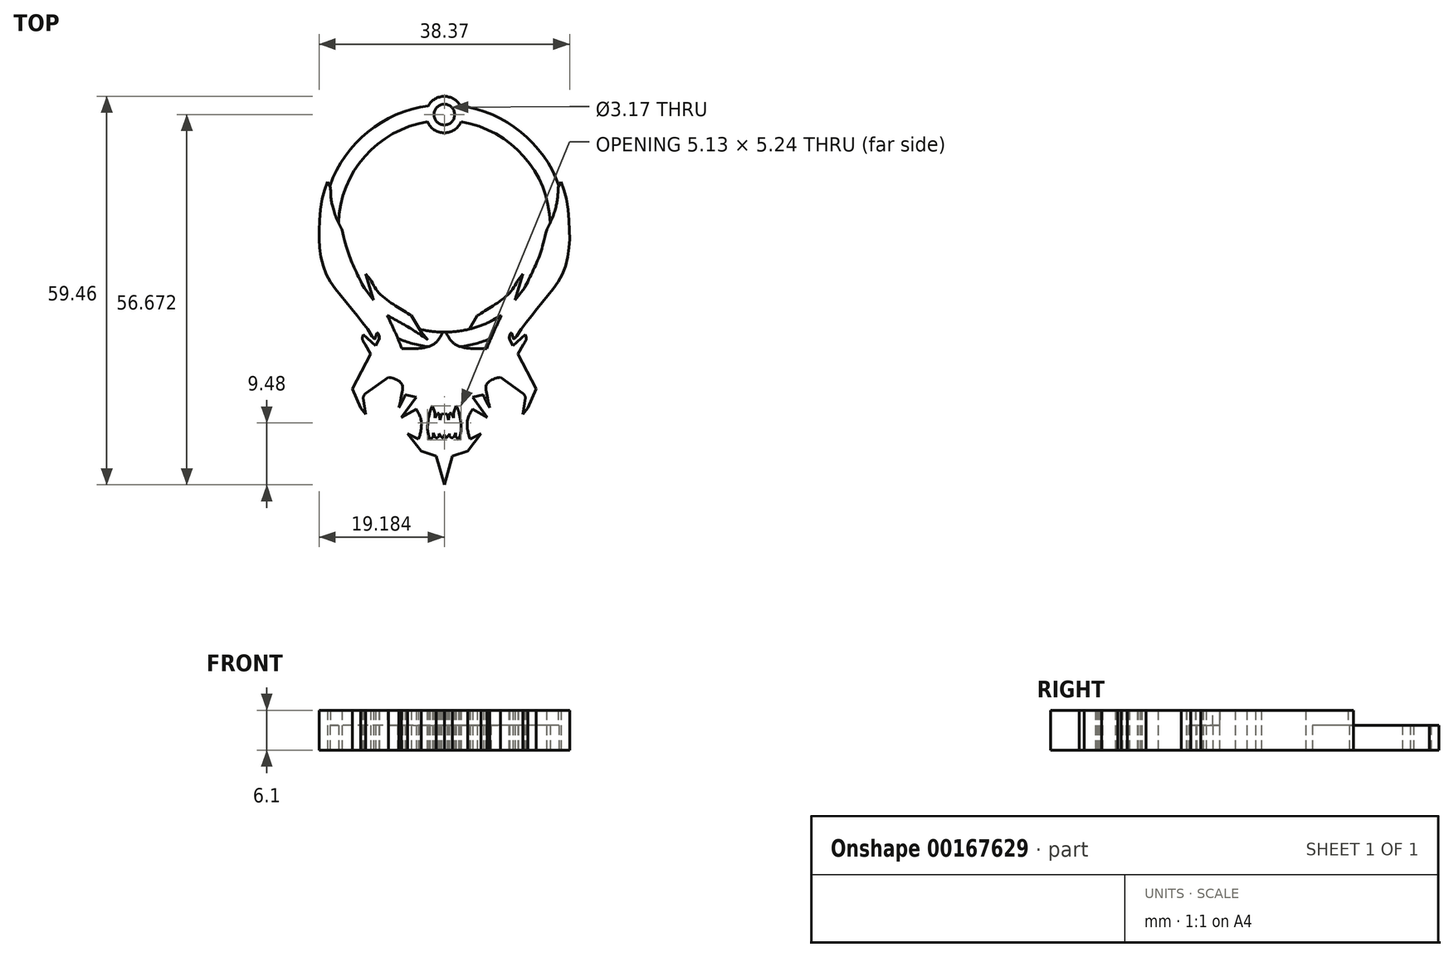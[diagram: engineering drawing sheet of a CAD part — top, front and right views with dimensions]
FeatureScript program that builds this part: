
annotation { "Feature Type Name" : "Feature", "Feature Type Description" : "" }
export const myFeature = defineFeature(function(context is Context, id is Id, definition is map)
    precondition{}
    {
        {
            var Q0;
            Q0=qCreatedBy(makeId("Top.planeOp"),FACE);
            var sketch = newSketch(context, id + "F0", { "sketchPlane" : qUnion([Q0])});
            skLineSegment(sketch, "E0", {"start": v(-0.9, 16.54) * mm, "end": v(-0.9, -34.26) * mm});
            skLineSegment(sketch, "E1", {"start": v(-18.76, 15.36) * mm, "end": v(-18.33, 14.53) * mm});
            skLineSegment(sketch, "E2", {"start": v(-12.92, 1.26) * mm, "end": v(-12.21, 0.39) * mm});
            skLineSegment(sketch, "E3", {"start": v(-5.97, -5.12) * mm, "end": v(-4.46, -7.6) * mm});
            skLineSegment(sketch, "E4", {"start": v(-4.46, -7.6) * mm, "end": v(-3.4, -8.82) * mm});
            skLineSegment(sketch, "E5", {"start": v(-13.17, -0.94) * mm, "end": v(-11.72, -2.75) * mm});
            skLineSegment(sketch, "E6", {"start": v(-11.72, -2.75) * mm, "end": v(-12.92, 1.26) * mm});
            skLineSegment(sketch, "E7", {"start": v(-11.4, -9.73) * mm, "end": v(-13.3, -8.03) * mm});
            skLineSegment(sketch, "E8", {"start": v(-11.4, -9.73) * mm, "end": v(-10.9, -8.8) * mm});
            skLineSegment(sketch, "E9", {"start": v(-12.99, -9.53) * mm, "end": v(-12.17, -10.97) * mm});
            skLineSegment(sketch, "E10", {"start": v(-12.17, -10.97) * mm, "end": v(-15, -16.37) * mm});
            skLineSegment(sketch, "E11", {"start": v(-15, -16.37) * mm, "end": v(-13.72, -19.25) * mm});
            skLineSegment(sketch, "E12", {"start": v(-13.72, -19.25) * mm, "end": v(-12.93, -20.2) * mm});
            skLineSegment(sketch, "E13", {"start": v(-12.93, -20.2) * mm, "end": v(-13.32, -17.75) * mm});
            skLineSegment(sketch, "E14", {"start": v(-7.49, -20.73) * mm, "end": v(-5.22, -19.47) * mm});
            skLineSegment(sketch, "E15", {"start": v(-6.52, -23.2) * mm, "end": v(-4.85, -24.02) * mm});
            skLineSegment(sketch, "E16", {"start": v(-6.52, -23.2) * mm, "end": v(-4.46, -25.88) * mm});
            skLineSegment(sketch, "E17", {"start": v(-4.46, -25.88) * mm, "end": v(-2.14, -26.62) * mm});
            skLineSegment(sketch, "E18", {"start": v(-2.14, -26.62) * mm, "end": v(-0.9, -31.03) * mm});
            skLineSegment(sketch, "E19", {"start": v(-7.49, -20.73) * mm, "end": v(-5.22, -17.58) * mm});
            skLineSegment(sketch, "E20", {"start": v(-12.93, -17.01) * mm, "end": v(-9.48, -14.56) * mm});
            skFitSpline(sketch, "E21", {"points": [v(-13.17, -0.94) * mm, v(-15, 2.9) * mm, v(-16.59, 8.02) * mm], "startDerivative": vector(-3.64, 7.42) * mm, "endDerivative": vector(-3.23, 13.75) * mm});
            skFitSpline(sketch, "E22", {"points": [v(-18.33, 14.53) * mm, v(-18.23, 12.72) * mm, v(-18.02, 11.67) * mm, v(-17.5, 10) * mm, v(-16.59, 8.02) * mm], "startDerivative": vector(0.21, -7.54) * mm, "endDerivative": vector(3.51, -6.9) * mm});
            skFitSpline(sketch, "E23", {"points": [v(-18.76, 15.36) * mm, v(-19.63, 12.59) * mm, v(-20.04, 8.55) * mm, v(-20.06, 5.8) * mm, v(-19.56, 2.84) * mm, v(-18.52, 0.36) * mm, v(-17, -1.75) * mm, v(-15.35, -3.78) * mm, v(-13.66, -5.91) * mm, v(-12.23, -7.87) * mm, v(-11.56, -8.74) * mm, v(-11.2, -7.77) * mm, v(-10.86, -8.3) * mm, v(-10.9, -8.8) * mm], "startDerivative": vector(-10.73, -28.25) * mm, "endDerivative": vector(-3.12, -11.1) * mm});
            skFitSpline(sketch, "E24", {"points": [v(-13.32, -17.75) * mm, v(-12.93, -17.01) * mm], "startDerivative": vector(0.06, 0.77) * mm, "endDerivative": vector(0.77, 0.6) * mm});
            skFitSpline(sketch, "E25", {"points": [v(-9.48, -14.56) * mm, v(-8.37, -14.86) * mm, v(-7.41, -15.6) * mm, v(-7.31, -16.57) * mm, v(-7.85, -19.21) * mm], "startDerivative": vector(4.95, -0.91) * mm, "endDerivative": vector(-1.96, -8.61) * mm});
            skFitSpline(sketch, "E26", {"points": [v(-7.85, -19.21) * mm, v(-6.9, -17.25) * mm, v(-6.22, -14.56) * mm, v(-5.62, -13.62) * mm, v(-5, -14.06) * mm, v(-4.16, -16.16) * mm], "startDerivative": vector(4.74, 8.02) * mm, "endDerivative": vector(3.29, -10.47) * mm});
            skFitSpline(sketch, "E27", {"points": [v(-4.16, -16.16) * mm, v(-4.16, -14.78) * mm, v(-3.84, -14.28) * mm, v(-3.1, -14.56) * mm, v(-2.34, -15.68) * mm], "startDerivative": vector(-0.38, 5.1) * mm, "endDerivative": vector(2.28, -4.33) * mm});
            skFitSpline(sketch, "E28", {"points": [v(-2.34, -15.68) * mm, v(-2.12, -14.3) * mm, v(-1.6, -14.36) * mm, v(-1.16, -15) * mm, v(-0.9, -16) * mm], "startDerivative": vector(0, 5.8) * mm, "endDerivative": vector(0.78, -3.9) * mm});
            skFitSpline(sketch, "E29", {"points": [v(-4, -18.46) * mm, v(-3.67, -17.81) * mm, v(-3.66, -17.58) * mm, v(-3.71, -17.39) * mm, v(-2.7, -17.39) * mm, v(-2.34, -17.58) * mm, v(-2.15, -17.58) * mm, v(-2.16, -16.45) * mm], "startDerivative": vector(2.63, 4.78) * mm, "endDerivative": vector(-0.92, 7.28) * mm});
            skFitSpline(sketch, "E30", {"points": [v(-2.16, -16.45) * mm, v(-1.77, -17.4) * mm, v(-1.06, -17.78) * mm, v(-0.9, -17.24) * mm], "startDerivative": vector(0.62, -2.51) * mm, "endDerivative": vector(0.37, 2.41) * mm});
            skFitSpline(sketch, "E31", {"points": [v(-3.35, -21) * mm, v(-3.47, -22.03) * mm, v(-3.42, -23.01) * mm, v(-3.1, -24.17) * mm], "startDerivative": vector(-0.42, -3.17) * mm, "endDerivative": vector(1.07, -3.34) * mm});
            skLineSegment(sketch, "E32", {"start": v(-3.1, -24.17) * mm, "end": v(-2.63, -23.65) * mm});
            skLineSegment(sketch, "E33", {"start": v(-2.63, -23.65) * mm, "end": v(-2.63, -23.06) * mm});
            skLineSegment(sketch, "E34", {"start": v(-2.63, -23.06) * mm, "end": v(-2.44, -23.6) * mm});
            skFitSpline(sketch, "E35", {"points": [v(-2.44, -23.6) * mm, v(-2.1, -23.82) * mm, v(-1.75, -23.6) * mm, v(-1.7, -23.22) * mm], "startDerivative": vector(0.93, -0.98) * mm, "endDerivative": vector(-0.09, 1.21) * mm});
            skFitSpline(sketch, "E36", {"points": [v(-1.7, -23.22) * mm, v(-1.44, -23.6) * mm, v(-1.18, -23.8) * mm, v(-0.9, -23.35) * mm], "startDerivative": vector(0.75, -1.1) * mm, "endDerivative": vector(0.71, 1.79) * mm});
            skLineSegment(sketch, "E37.MirrorCS", {"start": v(0.81, -23.06) * mm, "end": v(0.62, -23.6) * mm});
            skLineSegment(sketch, "E38.MirrorCS", {"start": v(0.81, -23.65) * mm, "end": v(0.81, -23.06) * mm});
            skLineSegment(sketch, "E39.MirrorCS", {"start": v(1.29, -24.17) * mm, "end": v(0.81, -23.65) * mm});
            skFitSpline(sketch, "E40.MirrorCS", {"points": [v(0.62, -23.6) * mm, v(0.3, -23.82) * mm, v(-0.06, -23.6) * mm, v(-0.1, -23.22) * mm], "startDerivative": vector(-0.93, -0.98) * mm, "endDerivative": vector(0.09, 1.21) * mm});
            skFitSpline(sketch, "E41.MirrorCS", {"points": [v(11.51, -17.75) * mm, v(11.12, -17.01) * mm], "startDerivative": vector(-0.06, 0.77) * mm, "endDerivative": vector(-0.77, 0.6) * mm});
            skFitSpline(sketch, "E42.MirrorCS", {"points": [v(2.18, -18.46) * mm, v(1.85, -17.81) * mm, v(1.85, -17.58) * mm, v(1.9, -17.39) * mm, v(0.88, -17.39) * mm, v(0.53, -17.58) * mm, v(0.33, -17.58) * mm, v(0.35, -16.45) * mm], "startDerivative": vector(-2.63, 4.78) * mm, "endDerivative": vector(0.92, 7.28) * mm});
            skLineSegment(sketch, "E43.MirrorCS", {"start": v(16.95, 15.36) * mm, "end": v(16.51, 14.53) * mm});
            skLineSegment(sketch, "E44.MirrorCS", {"start": v(11.12, -20.2) * mm, "end": v(11.51, -17.75) * mm});
            skFitSpline(sketch, "E45.MirrorCS", {"points": [v(2.35, -16.16) * mm, v(2.35, -14.78) * mm, v(2.03, -14.28) * mm, v(1.29, -14.56) * mm, v(0.53, -15.68) * mm], "startDerivative": vector(0.38, 5.1) * mm, "endDerivative": vector(-2.28, -4.33) * mm});
            skFitSpline(sketch, "E46.MirrorCS", {"points": [v(1.54, -21) * mm, v(1.65, -22.03) * mm, v(1.6, -23.01) * mm, v(1.29, -24.17) * mm], "startDerivative": vector(0.42, -3.17) * mm, "endDerivative": vector(-1.07, -3.34) * mm});
            skLineSegment(sketch, "E47.MirrorCS", {"start": v(11.9, -19.25) * mm, "end": v(11.12, -20.2) * mm});
            skLineSegment(sketch, "E48.MirrorCS", {"start": v(9.6, -9.73) * mm, "end": v(9.08, -8.8) * mm});
            skLineSegment(sketch, "E49.MirrorCS", {"start": v(11.36, -0.94) * mm, "end": v(9.9, -2.75) * mm});
            skLineSegment(sketch, "E50.MirrorCS", {"start": v(11.1, 1.26) * mm, "end": v(10.4, 0.39) * mm});
            skFitSpline(sketch, "E51.MirrorCS", {"points": [v(11.36, -0.94) * mm, v(13.2, 2.9) * mm, v(14.78, 8.02) * mm], "startDerivative": vector(3.64, 7.42) * mm, "endDerivative": vector(3.23, 13.75) * mm});
            skLineSegment(sketch, "E52.MirrorCS", {"start": v(4.7, -23.2) * mm, "end": v(3.04, -24.02) * mm});
            skFitSpline(sketch, "E53.MirrorCS", {"points": [v(7.67, -14.56) * mm, v(6.56, -14.86) * mm, v(5.6, -15.6) * mm, v(5.5, -16.57) * mm, v(6.04, -19.21) * mm], "startDerivative": vector(-4.95, -0.91) * mm, "endDerivative": vector(1.96, -8.61) * mm});
            skLineSegment(sketch, "E54.MirrorCS", {"start": v(5.67, -20.73) * mm, "end": v(3.4, -17.58) * mm});
            skLineSegment(sketch, "E55.MirrorCS", {"start": v(9.6, -9.73) * mm, "end": v(11.48, -8.03) * mm});
            skLineSegment(sketch, "E56.MirrorCS", {"start": v(2.64, -7.6) * mm, "end": v(1.59, -8.82) * mm});
            skLineSegment(sketch, "E57.MirrorCS", {"start": v(4.7, -23.2) * mm, "end": v(2.65, -25.88) * mm});
            skFitSpline(sketch, "E58.MirrorCS", {"points": [v(16.51, 14.53) * mm, v(16.42, 12.72) * mm, v(16.2, 11.67) * mm, v(15.7, 10) * mm, v(14.78, 8.02) * mm], "startDerivative": vector(-0.21, -7.54) * mm, "endDerivative": vector(-3.51, -6.9) * mm});
            skLineSegment(sketch, "E59.MirrorCS", {"start": v(13.18, -16.37) * mm, "end": v(11.9, -19.25) * mm});
            skLineSegment(sketch, "E60.MirrorCS", {"start": v(11.17, -9.53) * mm, "end": v(10.36, -10.97) * mm});
            skFitSpline(sketch, "E61.MirrorCS", {"points": [v(6.04, -19.21) * mm, v(5.08, -17.25) * mm, v(4.4, -14.56) * mm, v(3.8, -13.62) * mm, v(3.19, -14.06) * mm, v(2.35, -16.16) * mm], "startDerivative": vector(-4.74, 8.02) * mm, "endDerivative": vector(-3.29, -10.47) * mm});
            skLineSegment(sketch, "E62.MirrorCS", {"start": v(5.67, -20.73) * mm, "end": v(3.4, -19.47) * mm});
            skLineSegment(sketch, "E63.MirrorCS", {"start": v(11.12, -17.01) * mm, "end": v(7.67, -14.56) * mm});
            skLineSegment(sketch, "E64.MirrorCS", {"start": v(2.65, -25.88) * mm, "end": v(0.33, -26.62) * mm});
            skFitSpline(sketch, "E65.MirrorCS", {"points": [v(16.95, 15.36) * mm, v(17.82, 12.59) * mm, v(18.23, 8.55) * mm, v(18.24, 5.8) * mm, v(17.75, 2.84) * mm, v(16.71, 0.36) * mm, v(15.2, -1.75) * mm, v(13.54, -3.78) * mm, v(11.85, -5.91) * mm, v(10.42, -7.87) * mm, v(9.75, -8.74) * mm, v(9.38, -7.77) * mm, v(9.05, -8.3) * mm, v(9.08, -8.8) * mm], "startDerivative": vector(10.73, -28.25) * mm, "endDerivative": vector(3.12, -11.1) * mm});
            skLineSegment(sketch, "E66.MirrorCS", {"start": v(9.9, -2.75) * mm, "end": v(11.1, 1.26) * mm});
            skLineSegment(sketch, "E67.MirrorCS", {"start": v(4.16, -5.12) * mm, "end": v(2.64, -7.6) * mm});
            skLineSegment(sketch, "E68.MirrorCS", {"start": v(10.36, -10.97) * mm, "end": v(13.18, -16.37) * mm});
            skFitSpline(sketch, "E69.MirrorCS", {"points": [v(0.53, -15.68) * mm, v(0.3, -14.3) * mm, v(-0.2, -14.36) * mm, v(-0.65, -15) * mm, v(-0.9, -16) * mm], "startDerivative": vector(0, 5.8) * mm, "endDerivative": vector(-0.78, -3.9) * mm});
            skFitSpline(sketch, "E70.MirrorCS", {"points": [v(0.35, -16.45) * mm, v(-0.04, -17.4) * mm, v(-0.75, -17.78) * mm, v(-0.9, -17.24) * mm], "startDerivative": vector(-0.62, -2.51) * mm, "endDerivative": vector(-0.37, 2.41) * mm});
            skFitSpline(sketch, "E71.MirrorCS", {"points": [v(-0.1, -23.22) * mm, v(-0.37, -23.6) * mm, v(-0.63, -23.8) * mm, v(-0.9, -23.35) * mm], "startDerivative": vector(-0.75, -1.1) * mm, "endDerivative": vector(-0.71, 1.79) * mm});
            skFitSpline(sketch, "E72", {"points": [v(-5.22, -19.47) * mm, v(-4.47, -21.04) * mm, v(-4.55, -23.02) * mm, v(-4.85, -24.02) * mm], "startDerivative": vector(2.67, -4.13) * mm, "endDerivative": vector(-1.18, -3.25) * mm});
            skFitSpline(sketch, "E73.MirrorCS", {"points": [v(3.4, -19.47) * mm, v(2.66, -21.04) * mm, v(2.74, -23.02) * mm, v(3.04, -24.02) * mm], "startDerivative": vector(-2.67, -4.13) * mm, "endDerivative": vector(1.18, -3.25) * mm});
            skLineSegment(sketch, "E74.MirrorCS", {"start": v(0.33, -26.62) * mm, "end": v(-0.9, -31.03) * mm});
            skFitSpline(sketch, "E75", {"points": [v(-13.3, -8.03) * mm, v(-13.45, -8.7) * mm, v(-12.99, -9.53) * mm], "startDerivative": vector(-0.62, -1.45) * mm, "endDerivative": vector(1.2, -1.54) * mm});
            skFitSpline(sketch, "E76.MirrorCS", {"points": [v(11.48, -8.03) * mm, v(11.64, -8.7) * mm, v(11.17, -9.53) * mm], "startDerivative": vector(0.62, -1.45) * mm, "endDerivative": vector(-1.2, -1.54) * mm});
            skFitSpline(sketch, "E77", {"points": [v(-12.21, 0.39) * mm, v(-10.85, -1.7) * mm, v(-8.14, -3.78) * mm, v(-5.97, -5.12) * mm], "startDerivative": vector(3.54, -6.8) * mm, "endDerivative": vector(6.48, -3.95) * mm});
            skFitSpline(sketch, "E78.MirrorCS", {"points": [v(10.4, 0.39) * mm, v(9.04, -1.7) * mm, v(6.33, -3.78) * mm, v(4.16, -5.12) * mm], "startDerivative": vector(-3.54, -6.8) * mm, "endDerivative": vector(-6.48, -3.95) * mm});
            skFitSpline(sketch, "E79", {"points": [v(-3.4, -8.82) * mm, v(-6.27, -6.97) * mm, v(-9.65, -5.09) * mm], "startDerivative": vector(-5.78, 3.85) * mm, "endDerivative": vector(-6.72, 3.62) * mm});
            skFitSpline(sketch, "E80", {"points": [v(-9.65, -5.09) * mm, v(-8.37, -7.83) * mm, v(-7.4, -10.17) * mm], "startDerivative": vector(2.57, -5.34) * mm, "endDerivative": vector(1.9, -4.83) * mm});
            skFitSpline(sketch, "E81", {"points": [v(-7.4, -10.17) * mm, v(-5.45, -10.17) * mm, v(-2.53, -9.5) * mm, v(-0.9, -7.19) * mm], "startDerivative": vector(6.19, -0.16) * mm, "endDerivative": vector(3.64, 7.74) * mm});
            skFitSpline(sketch, "E82.MirrorCS", {"points": [v(1.59, -8.82) * mm, v(4.46, -6.97) * mm, v(7.84, -5.09) * mm], "startDerivative": vector(5.78, 3.85) * mm, "endDerivative": vector(6.72, 3.62) * mm});
            skFitSpline(sketch, "E83.MirrorCS", {"points": [v(7.84, -5.09) * mm, v(6.56, -7.83) * mm, v(5.6, -10.17) * mm], "startDerivative": vector(-2.57, -5.34) * mm, "endDerivative": vector(-1.9, -4.83) * mm});
            skFitSpline(sketch, "E84.MirrorCS", {"points": [v(5.6, -10.17) * mm, v(3.64, -10.17) * mm, v(0.72, -9.5) * mm, v(-0.9, -7.19) * mm], "startDerivative": vector(-6.19, -0.16) * mm, "endDerivative": vector(-3.64, 7.74) * mm});
            skLineSegment(sketch, "E85", {"start": v(-6.9, -17.25) * mm, "end": v(-5.22, -17.58) * mm});
            skLineSegment(sketch, "E86.MirrorCS", {"start": v(5.08, -17.25) * mm, "end": v(3.4, -17.58) * mm});
            skArc(sketch, "E87", {"start": v(-3.35, 26.98) * mm, "mid": v(-0.9, -10.05) * mm, "end": v(1.54, 26.98) * mm});
            skFitSpline(sketch, "E88", {"points": [v(-3.35, -21) * mm, v(-2.96, -19.39) * mm, v(-2.74, -18.93) * mm], "startDerivative": vector(0.6, 2.9) * mm, "endDerivative": vector(0.64, 1.05) * mm});
            skLineSegment(sketch, "E89", {"start": v(-2.74, -18.93) * mm, "end": v(-2.33, -20.01) * mm});
            skLineSegment(sketch, "E90", {"start": v(-2.33, -20.01) * mm, "end": v(-2.33, -20.78) * mm});
            skLineSegment(sketch, "E91", {"start": v(-2.33, -20.78) * mm, "end": v(-1.98, -20.08) * mm});
            skLineSegment(sketch, "E92", {"start": v(-1.98, -20.08) * mm, "end": v(-1.7, -20.08) * mm});
            skLineSegment(sketch, "E93", {"start": v(-1.7, -20.08) * mm, "end": v(-1.58, -21.08) * mm});
            skLineSegment(sketch, "E94", {"start": v(-1.58, -21.08) * mm, "end": v(-1.31, -20.11) * mm});
            skLineSegment(sketch, "E95", {"start": v(-1.31, -20.11) * mm, "end": v(-0.9, -20.23) * mm});
            skLineSegment(sketch, "E96.MirrorCS", {"start": v(-0.5, -20.11) * mm, "end": v(-0.9, -20.23) * mm});
            skLineSegment(sketch, "E97.MirrorCS", {"start": v(-0.23, -21.08) * mm, "end": v(-0.5, -20.11) * mm});
            skLineSegment(sketch, "E98.MirrorCS", {"start": v(-0.12, -20.08) * mm, "end": v(-0.23, -21.08) * mm});
            skLineSegment(sketch, "E99.MirrorCS", {"start": v(0.17, -20.08) * mm, "end": v(-0.12, -20.08) * mm});
            skLineSegment(sketch, "E100.MirrorCS", {"start": v(0.52, -20.78) * mm, "end": v(0.17, -20.08) * mm});
            skLineSegment(sketch, "E101.MirrorCS", {"start": v(0.52, -20.01) * mm, "end": v(0.52, -20.78) * mm});
            skLineSegment(sketch, "E102.MirrorCS", {"start": v(0.92, -18.93) * mm, "end": v(0.52, -20.01) * mm});
            skFitSpline(sketch, "E103.MirrorCS", {"points": [v(1.54, -21) * mm, v(1.15, -19.39) * mm, v(0.92, -18.93) * mm], "startDerivative": vector(-0.6, 2.9) * mm, "endDerivative": vector(-0.64, 1.05) * mm});
            skCircle(sketch, "E104", {"center": v(-0.9, 25.64) * mm, "radius": 1.59 * mm});
            skArc(sketch, "E105", {"start": v(-3.47, 24.54) * mm, "mid": v(-0.9, 22.85) * mm, "end": v(1.66, 24.54) * mm});
            skLineSegment(sketch, "E106", {"start": v(-9.65, -5.09) * mm, "end": v(-9.65, -5.09) * mm});
            skArc(sketch, "E107.trimOffspring", {"start": v(-4.7, -7.2) * mm, "mid": v(1.78, -7.42) * mm, "end": v(7.84, -5.09) * mm});
            skArc(sketch, "E108.trimOffspring", {"start": v(15.28, 9.04) * mm, "mid": v(11.26, 19.24) * mm, "end": v(1.66, 24.54) * mm});
            skArc(sketch, "E109.trimOffspring", {"start": v(-3.47, 24.54) * mm, "mid": v(-13.07, 19.24) * mm, "end": v(-17.1, 9.04) * mm});
            skArc(sketch, "E110.trimOffspring", {"start": v(1.54, 26.98) * mm, "mid": v(-0.9, 28.43) * mm, "end": v(-3.35, 26.98) * mm});
            skSolve(sketch);
        }
        {
            var Q0;
            Q0=makeQuery(id+"F0.imprint","IMPRINT",FACE,{"disambiguationData":[TD([[makeQuery(id+"F0.imprint","IMPRINT",EDGE,{"derivedFrom":sQuery(id+"F0.wireOp",EDGE,"E7")}),1.0]])]});
            var Q1;
            {var subQ1=sQuery(id+"F0.wireOp",EDGE,"E22");var subQ7=sQuery(id+"F0.wireOp",EDGE,"E1");var subQ9=makeQuery(id+"F0.imprint","INTERSECT",VERTEX,{"derivedFrom":[subQ7,subQ1]});Q1=makeQuery(id+"F0.imprint","IMPRINT",FACE,{"disambiguationData":[TD([[makeQuery(id+"F0.imprint","IMPRINT",EDGE,{"disambiguationData":[TD([[subQ9,1.0]])],"derivedFrom":subQ7}),-1.0]])]});}
            var Q2;
            Q2=makeQuery(id+"F0.imprint","IMPRINT",FACE,{"disambiguationData":[TD([[makeQuery(id+"F0.imprint","IMPRINT",EDGE,{"derivedFrom":sQuery(id+"F0.wireOp",EDGE,"E2")}),-1.0]])]});
            var Q3;
            {var subQ0=sQuery(id+"F0.wireOp",EDGE,"ihKO1U0Q-dlJt-CJ1A-9VKm-lVYREsdOOYFs");var subQ1=sQuery(id+"F0.wireOp",EDGE,"E0");var subQ2=makeQuery(id+"F0.imprint","INTERSECT",VERTEX,{"derivedFrom":[subQ1,subQ0]});Q3=makeQuery(id+"F0.imprint","IMPRINT",FACE,{"disambiguationData":[TD([[makeQuery(id+"F0.imprint","IMPRINT",EDGE,{"disambiguationData":[TD([[subQ2,-1.0]])],"derivedFrom":subQ1}),-1.0]])]});}
            var Q4;
            {var subQ1=sQuery(id+"F0.wireOp",EDGE,"E0");var subQ3=sQuery(id+"F0.wireOp",EDGE,"ihKO1U0Q-dlJt-CJ1A-9VKm-lVYREsdOOYFs");var subQ4=makeQuery(id+"F0.imprint","INTERSECT",VERTEX,{"derivedFrom":[subQ1,subQ3]});Q4=makeQuery(id+"F0.imprint","IMPRINT",FACE,{"disambiguationData":[TD([[makeQuery(id+"F0.imprint","IMPRINT",EDGE,{"disambiguationData":[TD([[subQ4,1.0]])],"derivedFrom":subQ3}),1.0]])]});}
            var Q5;
            {var subQ1=sQuery(id+"F0.wireOp",EDGE,"E0");var subQ3=sQuery(id+"F0.wireOp",EDGE,"ihKO1U0Q-dlJt-CJ1A-9VKm-lVYREsdOOYFs");var subQ4=makeQuery(id+"F0.imprint","INTERSECT",VERTEX,{"derivedFrom":[subQ1,subQ3]});Q5=makeQuery(id+"F0.imprint","IMPRINT",FACE,{"disambiguationData":[TD([[makeQuery(id+"F0.imprint","IMPRINT",EDGE,{"disambiguationData":[TD([[subQ4,-1.0]])],"derivedFrom":subQ3}),1.0]])]});}
            var Q6;
            {var subQ0=sQuery(id+"F0.wireOp",EDGE,"ihKO1U0Q-dlJt-CJ1A-9VKm-lVYREsdOOYFs");var subQ1=sQuery(id+"F0.wireOp",EDGE,"E0");var subQ2=makeQuery(id+"F0.imprint","INTERSECT",VERTEX,{"derivedFrom":[subQ1,subQ0]});Q6=makeQuery(id+"F0.imprint","IMPRINT",FACE,{"disambiguationData":[TD([[makeQuery(id+"F0.imprint","IMPRINT",EDGE,{"disambiguationData":[TD([[subQ2,-1.0]])],"derivedFrom":subQ1}),1.0]])]});}
            var Q7;
            Q7=makeQuery(id+"F0.imprint","IMPRINT",FACE,{"disambiguationData":[TD([[makeQuery(id+"F0.imprint","IMPRINT",EDGE,{"derivedFrom":sQuery(id+"F0.wireOp",EDGE,"E41.MirrorCS")}),-1.0]])]});
            var Q8;
            Q8=makeQuery(id+"F0.imprint","IMPRINT",FACE,{"disambiguationData":[TD([[makeQuery(id+"F0.imprint","IMPRINT",EDGE,{"derivedFrom":sQuery(id+"F0.wireOp",EDGE,"E49.MirrorCS")}),1.0]])]});
            var Q9;
            {var subQ1=sQuery(id+"F0.wireOp",EDGE,"E58.MirrorCS");var subQ7=sQuery(id+"F0.wireOp",EDGE,"E43.MirrorCS");var subQ9=makeQuery(id+"F0.imprint","INTERSECT",VERTEX,{"derivedFrom":[subQ7,subQ1]});Q9=makeQuery(id+"F0.imprint","IMPRINT",FACE,{"disambiguationData":[TD([[makeQuery(id+"F0.imprint","IMPRINT",EDGE,{"disambiguationData":[TD([[subQ9,1.0]])],"derivedFrom":subQ7}),1.0]])]});}
            var Q10;
            Q10=makeQuery(id+"F0.imprint","IMPRINT",FACE,{"disambiguationData":[TD([[makeQuery(id+"F0.imprint","IMPRINT",EDGE,{"derivedFrom":sQuery(id+"F0.wireOp",EDGE,"E14")}),1.0]])]});
            var Q11;
            Q11=makeQuery(id+"F0.imprint","IMPRINT",FACE,{"disambiguationData":[TD([[makeQuery(id+"F0.imprint","IMPRINT",EDGE,{"derivedFrom":sQuery(id+"F0.wireOp",EDGE,"E37.MirrorCS")}),1.0]])]});
            extrude(context, id + "F1", {"entities" : qUnion([Q0, Q1, Q2, Q3, Q4, Q5, Q6, Q7, Q8, Q9, Q10, Q11]), "depth" : 6.1 * mm});
        }
        {
            var Q0;
            {var subQ5=sQuery(id+"F0.wireOp",EDGE,"E22");var subQ6=sQuery(id+"F0.wireOp",EDGE,"E1");var subQ7=makeQuery(id+"F0.imprint","INTERSECT",VERTEX,{"derivedFrom":[subQ6,subQ5]});Q0=makeQuery(id+"F0.imprint","IMPRINT",FACE,{"disambiguationData":[TD([[makeQuery(id+"F0.imprint","IMPRINT",EDGE,{"disambiguationData":[TD([[subQ7,1.0]])],"derivedFrom":subQ6}),1.0]])]});}
            var Q1;
            {var subQ8=sQuery(id+"F0.wireOp",EDGE,"E79");var subQ9=sQuery(id+"F0.wireOp",EDGE,"E4");var subQ10=makeQuery(id+"F0.imprint","INTERSECT",VERTEX,{"derivedFrom":[subQ9,subQ8]});Q1=makeQuery(id+"F0.imprint","IMPRINT",FACE,{"disambiguationData":[TD([[makeQuery(id+"F0.imprint","IMPRINT",EDGE,{"disambiguationData":[TD([[subQ10,1.0]])],"derivedFrom":subQ9}),1.0]])]});}
            var Q2;
            {var subQ5=sQuery(id+"F0.wireOp",EDGE,"E56.MirrorCS");var subQ10=sQuery(id+"F0.wireOp",EDGE,"E82.MirrorCS");var subQ11=makeQuery(id+"F0.imprint","INTERSECT",VERTEX,{"derivedFrom":[subQ5,subQ10]});Q2=makeQuery(id+"F0.imprint","IMPRINT",FACE,{"disambiguationData":[TD([[makeQuery(id+"F0.imprint","IMPRINT",EDGE,{"disambiguationData":[TD([[subQ11,1.0]])],"derivedFrom":subQ5}),-1.0]])]});}
            var Q3;
            {var subQ0=sQuery(id+"F0.wireOp",EDGE,"E79");var subQ1=sQuery(id+"F0.wireOp",EDGE,"E4");var subQ2=makeQuery(id+"F0.imprint","INTERSECT",VERTEX,{"derivedFrom":[subQ1,subQ0]});Q3=makeQuery(id+"F0.imprint","IMPRINT",FACE,{"disambiguationData":[TD([[makeQuery(id+"F0.imprint","IMPRINT",EDGE,{"disambiguationData":[TD([[subQ2,1.0]])],"derivedFrom":subQ1}),-1.0]])]});}
            var Q4;
            {var subQ0=sQuery(id+"F0.wireOp",EDGE,"E82.MirrorCS");var subQ1=sQuery(id+"F0.wireOp",EDGE,"E56.MirrorCS");var subQ2=makeQuery(id+"F0.imprint","INTERSECT",VERTEX,{"derivedFrom":[subQ1,subQ0]});Q4=makeQuery(id+"F0.imprint","IMPRINT",FACE,{"disambiguationData":[TD([[makeQuery(id+"F0.imprint","IMPRINT",EDGE,{"disambiguationData":[TD([[subQ2,1.0]])],"derivedFrom":subQ1}),1.0]])]});}
            var Q5;
            {var subQ3=sQuery(id+"F0.wireOp",EDGE,"E43.MirrorCS");var subQ7=sQuery(id+"F0.wireOp",EDGE,"E58.MirrorCS");var subQ9=makeQuery(id+"F0.imprint","INTERSECT",VERTEX,{"derivedFrom":[subQ3,subQ7]});Q5=makeQuery(id+"F0.imprint","IMPRINT",FACE,{"disambiguationData":[TD([[makeQuery(id+"F0.imprint","IMPRINT",EDGE,{"disambiguationData":[TD([[subQ9,1.0]])],"derivedFrom":subQ3}),-1.0]])]});}
            var Q6;
            Q6=makeQuery(id+"F0.imprint","IMPRINT",FACE,{"disambiguationData":[TD([[makeQuery(id+"F0.imprint","IMPRINT",EDGE,{"derivedFrom":sQuery(id+"F0.wireOp",EDGE,"E104")}),-1.0]])]});
            extrude(context, id + "F2", {"entities" : qUnion([Q0, Q1, Q2, Q3, Q4, Q5, Q6]), "operationType" : NewBodyOperationType.ADD, "depth" : 3.8 * mm});
        }
    });
